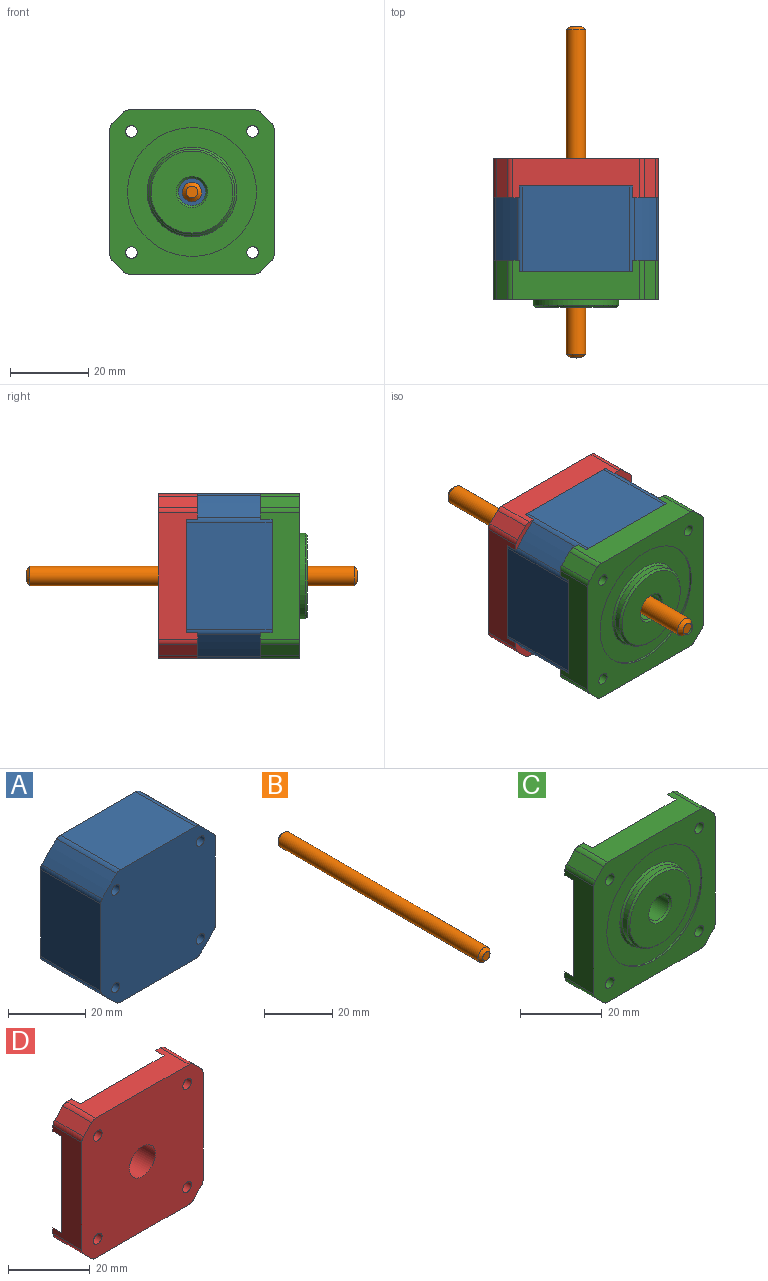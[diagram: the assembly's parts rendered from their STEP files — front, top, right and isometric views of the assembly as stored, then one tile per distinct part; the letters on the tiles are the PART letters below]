
ASSEMBLY  parts=4 mates=3
PART A: 22 faces, bbox 42x22x42 mm
  f0: cylinder r=55mm len=22mm, axis (0,1,0), area 169mm2, adj f8,f9,f10,f17
  f1: plane 27.54x22mm, normal (1,0,0), area 605.9mm2, adj f8,f9,f10,f11
  f2: cylinder r=55mm len=22mm, axis (0,1,0), area 169mm2, adj f8,f9,f11,f12
  f3: plane 27.54x22mm, normal (0,0,1), area 605.9mm2, adj f8,f9,f12,f13
  f4: cylinder r=55mm len=22mm, axis (0,1,0), area 169mm2, adj f8,f9,f13,f14
  f5: plane 27.54x22mm, normal (-1,0,0), area 605.9mm2, adj f8,f9,f14,f15
  f6: cylinder r=55mm len=22mm, axis (0,1,0), area 169mm2, adj f8,f9,f15,f16
  f7: plane 27.54x22mm, normal (0,0,-1), area 605.9mm2, adj f8,f9,f16,f17
  f8: plane 42x42mm, normal (0,-1,0), area 1655.7mm2, adj f0,f1,f2,f3,f4,f5,f6,f7
  f9: plane 42x42mm, normal (0,1,0), area 1655.7mm2, adj f0,f1,f2,f3,f4,f5,f6,f7
  f10: cylinder r=2mm len=22mm, axis (0,1,0), area 31.5mm2, adj f0,f1,f8,f9
  f11: cylinder r=2mm len=22mm, axis (0,1,0), area 31.5mm2, adj f1,f2,f8,f9
  f12: cylinder r=2mm len=22mm, axis (0,1,0), area 31.5mm2, adj f2,f3,f8,f9
  f13: cylinder r=2mm len=22mm, axis (0,1,0), area 31.5mm2, adj f3,f4,f8,f9
  f14: cylinder r=2mm len=22mm, axis (0,1,0), area 31.5mm2, adj f4,f5,f8,f9
  f15: cylinder r=2mm len=22mm, axis (0,1,0), area 31.5mm2, adj f5,f6,f8,f9
  f16: cylinder r=2mm len=22mm, axis (0,1,0), area 31.5mm2, adj f6,f7,f8,f9
  f17: cylinder r=2mm len=22mm, axis (0,1,0), area 31.5mm2, adj f0,f7,f8,f9
  f18: cylinder r=1.5mm len=22mm, axis (0,-1,0), area 207.3mm2, adj f8,f9
  f19: cylinder r=1.5mm len=22mm, axis (0,-1,0), area 207.3mm2, adj f8,f9
  f20: cylinder r=1.5mm len=22mm, axis (0,-1,0), area 207.3mm2, adj f8,f9
  f21: cylinder r=1.5mm len=22mm, axis (0,-1,0), area 207.3mm2, adj f8,f9
PART B: 5 faces, bbox 5x85x5 mm
  f0: cylinder r=2.5mm len=83mm, axis (0,1,0), area 1303.8mm2, adj f3,f4
  f1: plane 3x3mm, normal (0,-1,0), area 7.1mm2, adj f4
  f2: plane 3x3mm, normal (0,1,0), area 7.1mm2, adj f3
  f3: cone r=2.5mm half-angle=45deg, axis (0,-1,0), area 17.8mm2, adj f0,f2
  f4: cone r=1.5mm half-angle=45deg, axis (0,1,0), area 17.8mm2, adj f0,f1
PART C: 38 faces, bbox 42x12x42 mm
  f0: plane 32.34x10mm, normal (1,0,0), area 236.4mm2, adj f3,f4,f9,f20,f21,f29,f31,f32
  f1: plane 32.34x10mm, normal (0,0,1), area 236.4mm2, adj f2,f3,f9,f18,f19,f29,f30,f31
  f2: plane 6.49x6.49mm, normal (0,1,0), area 11.7mm2, adj f1,f7,f13,f19,f23,f30
  f3: plane 6.49x6.49mm, normal (0,1,0), area 11.7mm2, adj f0,f1,f12,f18,f21,f31
  f4: plane 6.49x6.49mm, normal (0,1,0), area 11.7mm2, adj f0,f8,f11,f20,f25,f32
  f5: plane 6.49x6.49mm, normal (0,1,0), area 11.7mm2, adj f7,f8,f10,f22,f24,f33
  f6: cylinder r=3.5mm len=8.5mm, axis (0,-1,0), area 186.9mm2, adj f27,f29
  f7: plane 32.34x10mm, normal (-1,0,0), area 236.4mm2, adj f2,f5,f9,f22,f23,f29,f30,f33
  f8: plane 32.34x10mm, normal (0,0,-1), area 236.4mm2, adj f4,f5,f9,f24,f25,f29,f32,f33
  f9: plane 42x42mm, normal (0,-1,0), area 847.7mm2, adj f0,f1,f7,f8,f10,f11,f12,f13
  f10: plane 10x2.83mm, normal (-0.71,0,-0.71), area 40mm2, adj f5,f9,f22,f24
  f11: plane 10x2.83mm, normal (0.71,0,-0.71), area 40mm2, adj f4,f9,f20,f25
  f12: plane 10x2.83mm, normal (0.71,0,0.71), area 40mm2, adj f3,f9,f18,f21
  f13: plane 10x2.83mm, normal (-0.71,0,0.71), area 40mm2, adj f2,f9,f19,f23
  f14: cylinder r=16.5mm len=33mm, axis (0,-1,0), area 51.8mm2, adj f9,f15
  f15: plane 33x33mm, normal (0,-1,0), area 439.8mm2, adj f14,f26
  f16: cylinder r=11mm len=22mm, axis (0,1,0), area 103.7mm2, adj f26,f28
  f17: plane 21x21mm, normal (0,-1,0), area 296.1mm2, adj f27,f28
  f18: cylinder r=2mm len=10mm, axis (0,-1,0), area 15.7mm2, adj f1,f3,f9,f12
  f19: cylinder r=2mm len=10mm, axis (0,-1,0), area 15.7mm2, adj f1,f2,f9,f13
  f20: cylinder r=2mm len=10mm, axis (0,1,0), area 15.7mm2, adj f0,f4,f9,f11
  f21: cylinder r=2mm len=10mm, axis (0,1,0), area 15.7mm2, adj f0,f3,f9,f12
  f22: cylinder r=2mm len=10mm, axis (0,-1,0), area 15.7mm2, adj f5,f7,f9,f10
  f23: cylinder r=2mm len=10mm, axis (0,-1,0), area 15.7mm2, adj f2,f7,f9,f13
  f24: cylinder r=2mm len=10mm, axis (0,1,0), area 15.7mm2, adj f5,f8,f9,f10
  f25: cylinder r=2mm len=10mm, axis (0,1,0), area 15.7mm2, adj f4,f8,f9,f11
  f26: cone r=11mm half-angle=45deg, axis (0,1,0), area 50mm2, adj f15,f16
  f27: cone r=3.5mm half-angle=45deg, axis (0,-1,0), area 16.7mm2, adj f6,f17
  f28: cone r=10.5mm half-angle=45deg, axis (0,1,0), area 47.8mm2, adj f16,f17
  f29: plane 42x42mm, normal (0,1,0), area 1617.7mm2, adj f0,f1,f6,f7,f8,f30,f31,f32
  f30: cylinder r=55mm len=6.49mm, axis (0,1,0), area 27.6mm2, adj f1,f2,f7,f29
  f31: cylinder r=55mm len=6.49mm, axis (0,1,0), area 27.6mm2, adj f0,f1,f3,f29
  f32: cylinder r=55mm len=6.49mm, axis (0,1,0), area 27.6mm2, adj f0,f4,f8,f29
  f33: cylinder r=55mm len=6.49mm, axis (0,1,0), area 27.6mm2, adj f5,f7,f8,f29
  f34: cylinder r=1.5mm len=7mm, axis (0,-1,0), area 66mm2, adj f9,f29
  f35: cylinder r=1.5mm len=7mm, axis (0,-1,0), area 66mm2, adj f9,f29
  f36: cylinder r=1.5mm len=7mm, axis (0,-1,0), area 66mm2, adj f9,f29
  f37: cylinder r=1.5mm len=7mm, axis (0,-1,0), area 66mm2, adj f9,f29
PART D: 31 faces, bbox 42x10x42 mm
  f0: plane 32.34x10mm, normal (1,0,0), area 236.4mm2, adj f3,f4,f8,f15,f16,f22,f23,f25
  f1: plane 32.34x10mm, normal (0,0,1), area 236.4mm2, adj f2,f3,f8,f13,f14,f21,f22,f25
  f2: plane 6.49x6.49mm, normal (0,1,0), area 11.7mm2, adj f1,f6,f12,f14,f18,f21
  f3: plane 6.49x6.49mm, normal (0,1,0), area 11.7mm2, adj f0,f1,f11,f13,f16,f22
  f4: plane 6.49x6.49mm, normal (0,1,0), area 11.7mm2, adj f0,f7,f10,f15,f20,f23
  f5: plane 6.49x6.49mm, normal (0,1,0), area 11.7mm2, adj f6,f7,f9,f17,f19,f24
  f6: plane 32.34x10mm, normal (-1,0,0), area 236.4mm2, adj f2,f5,f8,f17,f18,f21,f24,f25
  f7: plane 32.34x10mm, normal (0,0,-1), area 236.4mm2, adj f4,f5,f8,f19,f20,f23,f24,f25
  f8: plane 42x42mm, normal (0,-1,0), area 1639.4mm2, adj f0,f1,f6,f7,f9,f10,f11,f12
  f9: plane 10x2.83mm, normal (-0.71,0,-0.71), area 40mm2, adj f5,f8,f17,f19
  f10: plane 10x2.83mm, normal (0.71,0,-0.71), area 40mm2, adj f4,f8,f15,f20
  f11: plane 10x2.83mm, normal (0.71,0,0.71), area 40mm2, adj f3,f8,f13,f16
  f12: plane 10x2.83mm, normal (-0.71,0,0.71), area 40mm2, adj f2,f8,f14,f18
  f13: cylinder r=2mm len=10mm, axis (0,-1,0), area 15.7mm2, adj f1,f3,f8,f11
  f14: cylinder r=2mm len=10mm, axis (0,-1,0), area 15.7mm2, adj f1,f2,f8,f12
  f15: cylinder r=2mm len=10mm, axis (0,1,0), area 15.7mm2, adj f0,f4,f8,f10
  f16: cylinder r=2mm len=10mm, axis (0,1,0), area 15.7mm2, adj f0,f3,f8,f11
  f17: cylinder r=2mm len=10mm, axis (0,-1,0), area 15.7mm2, adj f5,f6,f8,f9
  f18: cylinder r=2mm len=10mm, axis (0,-1,0), area 15.7mm2, adj f2,f6,f8,f12
  f19: cylinder r=2mm len=10mm, axis (0,1,0), area 15.7mm2, adj f5,f7,f8,f9
  f20: cylinder r=2mm len=10mm, axis (0,1,0), area 15.7mm2, adj f4,f7,f8,f10
  f21: cylinder r=55mm len=6.49mm, axis (0,1,0), area 27.6mm2, adj f1,f2,f6,f25
  f22: cylinder r=55mm len=6.49mm, axis (0,1,0), area 27.6mm2, adj f0,f1,f3,f25
  f23: cylinder r=55mm len=6.49mm, axis (0,1,0), area 27.6mm2, adj f0,f4,f7,f25
  f24: cylinder r=55mm len=6.49mm, axis (0,1,0), area 27.6mm2, adj f5,f6,f7,f25
  f25: plane 42x42mm, normal (0,1,0), area 1592.6mm2, adj f0,f1,f6,f7,f21,f22,f23,f24
  f26: cylinder r=1.5mm len=7mm, axis (0,-1,0), area 66mm2, adj f8,f25
  f27: cylinder r=1.5mm len=7mm, axis (0,-1,0), area 66mm2, adj f8,f25
  f28: cylinder r=1.5mm len=7mm, axis (0,-1,0), area 66mm2, adj f8,f25
  f29: cylinder r=1.5mm len=7mm, axis (0,-1,0), area 66mm2, adj f8,f25
  f30: cylinder r=4.5mm len=9mm, axis (0,-1,0), area 197.9mm2, adj f8,f25
PLACE A t=(1.6,15.94,1.53)mm
PLACE B t=(1.6,25.44,1.53)mm
PLACE C t=(1.6,7.94,1.53)mm fixed
PLACE D rot(axis=(0,0,1),180deg) t=(1.6,23.94,1.53)mm
MATE fastened A.f19 <-> C.f34  axis (0,-1,0) through (-13.9,4.94,17.03)mm
MATE revolute B.f0 <-> C.f6  axis (0,-1,0) through (1.6,-17.06,1.53)mm
MATE fastened D.f29 <-> A.f19  axis (0,-1,0) through (-13.9,26.94,17.03)mm
